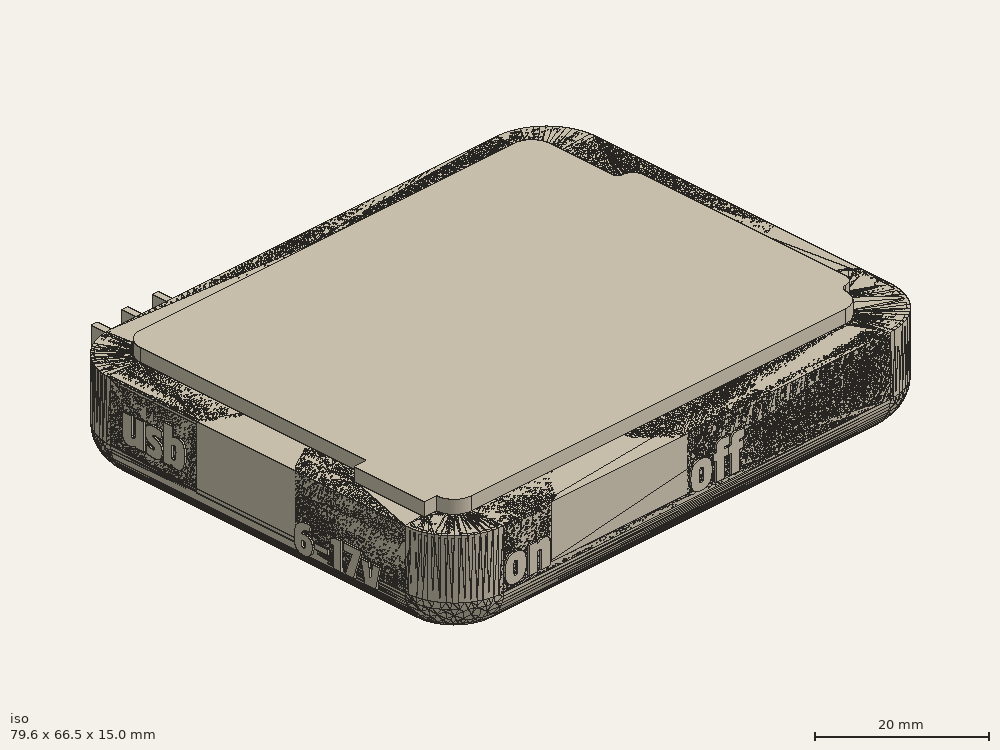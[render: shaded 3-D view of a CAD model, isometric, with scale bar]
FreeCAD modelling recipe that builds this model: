
FCSTD DOCUMENT  (FreeCAD 0.16R6712 (Git))
Label: baseConLetras
License: All rights reserved
LicenseURL: http://en.wikipedia.org/wiki/All_rights_reserved
objects: PartDesign::Fillet×18, Sketcher::SketchObject×15, PartDesign::Pocket×9, Part::Extrusion×7, PartDesign::Pad×6, Part::MultiFuse×6, Part::Cylinder×4, Part::Box×3, PartDesign::Chamfer×2, Part::Cut×1, Mesh::Feature×1, Part::Feature×1, Part::FeaturePython×1, Part::Mirroring×1
note: 89 computed .brp shape members not serialized (recipe doc carries the construction recipe); baked Part::Feature solids carry a one-line shape summary decoded from their .brp

FEATURE [Part::Cylinder] Cylinder  label="Cilindro"
  Angle = 360
  Height = 4.5
  Placement = pos=(-20.32,-24.13,0) rot=(0,0,1;0rad)
  Radius = 1.4
FEATURE [Part::Cylinder] Cylinder001  label="Cilindro001"
  Angle = 360
  Height = 4.5
  Placement = pos=(31.75,-19.05,0) rot=(0,0,1;0rad)
  Radius = 1.4
FEATURE [Part::Cylinder] Cylinder002  label="Cilindro002"
  Angle = 360
  Height = 4.5
  Placement = pos=(31.75,8.9,0) rot=(0,0,1;0rad)
  Radius = 1.4
FEATURE [Part::Cylinder] Cylinder003  label="Cilindro003"
  Angle = 360
  Height = 4.5
  Placement = pos=(-19.05,24.13,0) rot=(0,0,1;0rad)
  Radius = 1.4
FEATURE [Sketcher::SketchObject] Sketch
  Placement = pos=(0,0,3) rot=(0,0,1;0rad)
  sketch-geometry (16):
    g0: LineSegment StartX=-34.59 StartY=-24.13 StartZ=0 EndX=-36.59 EndY=-24.13 EndZ=0
    g1: LineSegment StartX=-36.59 StartY=-24.13 StartZ=0 EndX=-36.59 EndY=-12.63 EndZ=0
    g2: LineSegment StartX=-36.59 StartY=-12.63 StartZ=0 EndX=-34.59 EndY=-12.63 EndZ=0
    g3: LineSegment StartX=-34.59 StartY=-12.63 StartZ=0 EndX=-34.59 EndY=24.13 EndZ=0
    g4: ArcOfCircle CenterX=-31.75 CenterY=24.13 CenterZ=0 NormalX=0 NormalY=0 NormalZ=1 Radius=2.84 StartAngle=1.5708 EndAngle=3.14159
    g5: LineSegment StartX=-31.75 StartY=26.97 StartZ=0 EndX=29.21 EndY=26.97 EndZ=0
    g6: ArcOfCircle CenterX=29.21 CenterY=24.13 CenterZ=0 NormalX=0 NormalY=0 NormalZ=1 Radius=2.84 StartAngle=3.7035e-08 EndAngle=1.5708
    g7: LineSegment StartX=32.05 StartY=24.13 StartZ=0 EndX=32.05 EndY=13.97 EndZ=0
    g8: ArcOfCircle CenterX=33.02 CenterY=13.97 CenterZ=0 NormalX=0 NormalY=0 NormalZ=1 Radius=0.969997 StartAngle=3.14159 EndAngle=4.71239
    g9: ArcOfCircle CenterX=33.02 CenterY=11.43 CenterZ=0 NormalX=0 NormalY=0 NormalZ=1 Radius=1.57 StartAngle=6.28319 EndAngle=7.85398
    g10: LineSegment StartX=34.59 StartY=11.43 StartZ=0 EndX=34.59 EndY=-21.59 EndZ=0
    g11: ArcOfCircle CenterX=33.02 CenterY=-21.59 CenterZ=0 NormalX=0 NormalY=0 NormalZ=1 Radius=1.57 StartAngle=4.71239 EndAngle=6.28319
    g12: ArcOfCircle CenterX=33.02 CenterY=-24.13 CenterZ=0 NormalX=0 NormalY=0 NormalZ=1 Radius=0.97 StartAngle=1.5708 EndAngle=3.1416
    g13: ArcOfCircle CenterX=29.21 CenterY=-24.13 CenterZ=0 NormalX=0 NormalY=0 NormalZ=1 Radius=2.83999 StartAngle=4.71238 EndAngle=6.28319
    g14: LineSegment StartX=29.21 StartY=-26.97 StartZ=0 EndX=-31.75 EndY=-26.97 EndZ=0
    g15: ArcOfCircle CenterX=-31.75 CenterY=-24.13 CenterZ=0 NormalX=0 NormalY=0 NormalZ=1 Radius=2.84 StartAngle=3.14159 EndAngle=4.71239
  constraints (56):
    c: Horizontal(g0)
    c: Coincident(g0,g1)
    c: Vertical(g1)
    c: Coincident(g1,g2)
    c: Horizontal(g2)
    c: Coincident(g2,g3)
    c: Vertical(g3)
    c: Coincident(g4,g3)
    c: DistanceY(g2,g-1) = 12.63
    c: DistanceX(g2,g-1) = 34.59
    c: DistanceY(g-1,g3) = 24.13
    c: Tangent(g3,g4)
    c: DistanceY(g-1,g4) = 26.97
    c: DistanceX(g2,g2) = 2
    c: DistanceY(g1,g1) = 11.5
    c: DistanceX(g0,g0) = 2
    c: Coincident(g5,g4)
    c: Horizontal(g5)
    c: DistanceX(g5,g5) = 60.96
    c: Tangent(g4,g5)
    c: Coincident(g6,g5)
    c: Tangent(g6,g5)
    c: DistanceY(g-1,g6) = 24.13
    c: Coincident(g7,g6)
    c: Vertical(g7)
    c: DistanceY(g7,g7) = 10.16
    c: Tangent(g7,g6)
    c: Coincident(g8,g7)
    c: Coincident(g9,g8)
    c: Tangent(g8,g9)
    c: Tangent(g8,g7)
    c: Coincident(g10,g9)
    c: Vertical(g10)
    c: DistanceX(g-1,g10) = 34.59
    c: DistanceY(g10,g-1) = 21.59
    c: Tangent(g10,g9)
    c: DistanceY(g-1,g9) = 11.43
    c: Coincident(g11,g10)
    c: Coincident(g12,g11)
    c: Coincident(g13,g12)
    c: Tangent(g11,g12)
    c: Tangent(g11,g10)
    c: Tangent(g13,g12)
    c: DistanceX(g7,g8) = 0.97
    c: DistanceX(g11,g10) = 1.57
    c: DistanceX(g12,g11) = 0.97
    c: Radius(g11) = 1.57
    c: DistanceY(g13,g-1) = 26.97
    c: Coincident(g14,g13)
    c: Horizontal(g14)
    c: DistanceX(g14,g-1) = 31.75
    c: Coincident(g15,g14)
    c: Coincident(g15,g0)
    c: Radius(g15) = 2.84
    c: DistanceX(g-1,g13) = 29.21
    c: Tangent(g14,g13)
FEATURE [PartDesign::Pad] Pad  label="placa"
  Length = 10
  Length2 = 100
  Placement = pos=(0,0,3) rot=(0,0,1;0rad)
  Sketch = -> Sketch
  Type = 0
FEATURE [Sketcher::SketchObject] Sketch001
  ExternalGeometry = -> [Pad]
  Placement = pos=(0,0,3) rot=(1,0,0;3.14159rad)
  Support = -> Pad [Face17]
  sketch-geometry (24):
    g0: ArcOfCircle CenterX=29.21 CenterY=24.13 CenterZ=0 NormalX=0 NormalY=0 NormalZ=1 Radius=1.5 StartAngle=6.28318 EndAngle=7.85398
    g1: ArcOfCircle CenterX=31.77 CenterY=19.04 CenterZ=0 NormalX=0 NormalY=0 NormalZ=1 Radius=3 StartAngle=2.27479 EndAngle=4.23644
    g2: ArcOfCircle CenterX=-20.32 CenterY=24.13 CenterZ=0 NormalX=0 NormalY=0 NormalZ=1 Radius=3 StartAngle=3.32443 EndAngle=6.10035
    g3: ArcOfCircle CenterX=-14.9117 CenterY=23.13 CenterZ=0 NormalX=0 NormalY=0 NormalZ=1 Radius=2.5 StartAngle=1.5708 EndAngle=2.95876
    g4: LineSegment StartX=-14.9117 StartY=25.63 StartZ=0 EndX=29.21 EndY=25.63 EndZ=0
    g5: ArcOfCircle CenterX=-31.75 CenterY=24.13 CenterZ=0 NormalX=0 NormalY=0 NormalZ=1 Radius=1.50001 StartAngle=1.5708 EndAngle=3.14159
    g6: LineSegment StartX=-31.75 StartY=25.63 StartZ=0 EndX=-25.7283 EndY=25.63 EndZ=0
    g7: ArcOfCircle CenterX=-25.7283 CenterY=23.13 CenterZ=0 NormalX=0 NormalY=0 NormalZ=1 Radius=2.5 StartAngle=0.182833 EndAngle=1.5708
    g8: LineSegment StartX=-33.25 StartY=24.13 StartZ=0 EndX=-33.25 EndY=-24.13 EndZ=0
    g9: ArcOfCircle CenterX=-31.75 CenterY=-24.13 CenterZ=0 NormalX=0 NormalY=0 NormalZ=1 Radius=1.50001 StartAngle=3.14159 EndAngle=4.71239
    g10: ArcOfCircle CenterX=-19.05 CenterY=-24.13 CenterZ=0 NormalX=0 NormalY=0 NormalZ=1 Radius=3 StartAngle=0.182835 EndAngle=2.95876
    g11: ArcOfCircle CenterX=-24.4583 CenterY=-23.13 CenterZ=0 NormalX=0 NormalY=0 NormalZ=1 Radius=2.5 StartAngle=4.71239 EndAngle=6.10035
    g12: LineSegment StartX=-31.75 StartY=-25.63 StartZ=0 EndX=-24.4583 EndY=-25.63 EndZ=0
    g13: ArcOfCircle CenterX=-13.6417 CenterY=-23.13 CenterZ=0 NormalX=0 NormalY=0 NormalZ=1 Radius=2.5 StartAngle=3.32443 EndAngle=4.71239
    g14: LineSegment StartX=-13.6417 StartY=-25.63 StartZ=0 EndX=29.21 EndY=-25.63 EndZ=0
    g15: ArcOfCircle CenterX=29.21 CenterY=-24.13 CenterZ=0 NormalX=0 NormalY=0 NormalZ=1 Radius=1.5 StartAngle=4.71239 EndAngle=6.28319
    g16: ArcOfCircle CenterX=31.75 CenterY=-8.9 CenterZ=0 NormalX=0 NormalY=0 NormalZ=1 Radius=3 StartAngle=2.04266 EndAngle=4.01315
    g17: ArcOfCircle CenterX=28.21 CenterY=-13.1093 CenterZ=0 NormalX=0 NormalY=0 NormalZ=1 Radius=2.5 StartAngle=6.2812e-08 EndAngle=0.871554
    g18: LineSegment StartX=30.71 StartY=-24.13 StartZ=0 EndX=30.71 EndY=-13.1093 EndZ=0
    g19: ArcOfCircle CenterX=29.25 CenterY=-4.00102 CenterZ=0 NormalX=0 NormalY=0 NormalZ=1 Radius=2.5 StartAngle=5.18425 EndAngle=6.28319
    g20: ArcOfCircle CenterX=29.25 CenterY=14.1513 CenterZ=0 NormalX=0 NormalY=0 NormalZ=1 Radius=2.5 StartAngle=6.28319 EndAngle=7.37804
    g21: LineSegment StartX=31.75 StartY=14.1513 StartZ=0 EndX=31.75 EndY=-4.00102 EndZ=0
    g22: LineSegment StartX=30.71 StartY=24.13 StartZ=0 EndX=30.71 EndY=23.2324 EndZ=0
    g23: ArcOfCircle CenterX=28.21 CenterY=23.2324 CenterZ=0 NormalX=0 NormalY=0 NormalZ=1 Radius=2.5 StartAngle=5.41639 EndAngle=6.28318
  constraints (84):
    c: Coincident(g0,g-3)
    c: Radius(g1) = 3
    c: Radius(g0) = 1.5
    c: DistanceY(g1,g-4) = 2.55
    c: DistanceX(g1,g-4) = 2.82
    c: DistanceY(g-1,g2) = 24.13
    c: DistanceX(g2,g-1) = 20.32
    c: Radius(g2) = 3
    c: Coincident(g3,g2)
    c: Coincident(g4,g3)
    c: Coincident(g4,g0)
    c: Horizontal(g4)
    c: Tangent(g4,g0)
    c: Tangent(g3,g4)
    c: Tangent(g2,g3)
    c: Radius(g3) = 2.5
    c: Coincident(g5,g-6)
    c: PointOnObject(g5,g4)
    c: Tangent(g5,g4) = 1.5708
    c: Coincident(g6,g5)
    c: Horizontal(g6)
    c: Coincident(g7,g2)
    c: Coincident(g7,g6)
    c: Tangent(g7,g2)
    c: Tangent(g6,g7)
    c: Radius(g7) = 2.5
    c: Coincident(g8,g5)
    c: Vertical(g8)
    c: Coincident(g9,g-7)
    c: Coincident(g9,g8)
    c: Tangent(g9,g8)
    c: Tangent(g5,g8)
    c: DistanceY(g10,g-1) = 24.13
    c: DistanceX(g10,g-1) = 19.05
    c: Radius(g10) = 3
    c: Coincident(g11,g10)
    c: Coincident(g12,g9)
    c: Coincident(g12,g11)
    c: Horizontal(g12)
    c: Tangent(g9,g12)
    c: Tangent(g12,g11)
    c: Tangent(g11,g10)
    c: Radius(g11) = 2.5
    c: Coincident(g13,g10)
    c: Tangent(g13,g10)
    c: Coincident(g14,g13)
    c: Horizontal(g14)
    c: Coincident(g15,g-8)
    c: Coincident(g15,g14)
    c: Coincident(g17,g16)
    c: Tangent(g15,g14)
    c: Tangent(g14,g13)
    c: Radius(g15) = 1.5
    c: Radius(g13) = 2.5
    c: Coincident(g18,g15)
    c: Coincident(g18,g17)
    c: Vertical(g18)
    c: Tangent(g15,g18)
    c: DistanceX(g-1,g16) = 31.75
    c: DistanceY(g16,g-1) = 8.9
    c: Tangent(g16,g17)
    c: Tangent(g17,g18)
    c: Radius(g16) = 3
    c: Coincident(g19,g16)
    c: Coincident(g20,g1)
    c: Coincident(g21,g20)
    c: Coincident(g21,g19)
    c: Vertical(g21)
    c: Tangent(g19,g21)
    c: Tangent(g19,g16)
    c: Radius(g19) = 2.5
    c: Radius(g17) = 2.5
    c: Tangent(g20,g21)
    c: Tangent(g20,g1)
    c: Radius(g20) = 2.5
    c: DistanceX(g-1,g20) = 31.75
    c: Coincident(g22,g0)
    c: Vertical(g22)
    c: Tangent(g22,g0)
    c: Coincident(g23,g1)
    c: Coincident(g23,g22)
    c: Tangent(g23,g22)
    c: Tangent(g23,g1)
    c: Radius(g23) = 2.5
FEATURE [PartDesign::Pad] Pad001
  Length = 4
  Length2 = 100
  Placement = pos=(0,0,3) rot=(0,0,1;0rad)
  Sketch = -> Sketch001
  Type = 0
FEATURE [Part::Box] Box  label="Cubo"
  Height = 13
  Length = 79
  Placement = pos=(-39.6,-32,-2) rot=(0,0,1;0rad)
  Width = 64
FEATURE [PartDesign::Fillet] Fillet
  Base = -> Box [Edge7,Edge3,Edge5,Edge1]
  Placement = pos=(-39.6,-32,-2) rot=(0,0,1;0rad)
  Radius = 8
FEATURE [Part::Cut] Cut
  Base = -> Fillet
  Tool = -> Pad001
FEATURE [PartDesign::Chamfer] Chamfer
  Base = -> Cut [Edge4,Edge28,Edge30,Edge32,Edge33,Edge34,Edge35,Edge36]
  Size = 2
FEATURE [PartDesign::Fillet] Fillet001
  Base = -> Chamfer [Edge37,Edge5,Edge2,Edge33,Edge49,Edge51,Edge52,Edge46]
  Radius = 5
FEATURE [PartDesign::Fillet] Fillet002
  Base = -> Fillet001 [Edge155,Edge152,Edge151,Edge148,Edge147,Edge144,Edge143,Edge141,Edge139,Edge137,Edge135,Edge132,Edge130,Edge176,Edge175,Edge173,Edge171,Edge168,Edge167,Edge164,Edge163,Edge160,Edge159,Edge156]
  Radius = 2
FEATURE [PartDesign::Fillet] Fillet003
  Base = -> Fillet002 [Edge83,Edge76,Edge74,Edge79]
  Radius = 0.5
FEATURE [Part::MultiFuse] Fusion
  Shapes = -> [Cylinder003,Cylinder002,Cylinder001,Cylinder]
FEATURE [PartDesign::Fillet] Fillet004  label="tetones"
  Base = -> Fusion [Edge4,Edge10,Edge7,Edge1]
  Radius = 0.5
FEATURE [Mesh::Feature] Icezum_Alhambra_Support_with_text  label="Icezum-Alhambra-Support-with-text"
FEATURE [Part::Feature] Icezum_Alhambra_Support_with_text001
  shape: bbox 75.21 x 82 x 7 mm, 5620 faces, 0 solids (baked)
FEATURE [Sketcher::SketchObject] Sketch002
  Placement = pos=(0,0,11) rot=(0,0,1;0rad)
  Support = -> Fillet003 [Face46]
  sketch-geometry (4):
    g0: LineSegment StartX=-40 StartY=10 StartZ=0 EndX=-33 EndY=6 EndZ=0
    g1: LineSegment StartX=-33 StartY=6 StartZ=0 EndX=-33 EndY=-2 EndZ=0
    g2: LineSegment StartX=-33 StartY=-2 StartZ=0 EndX=-40 EndY=-6 EndZ=0
    g3: LineSegment StartX=-40 StartY=-6 StartZ=0 EndX=-40 EndY=10 EndZ=0
  constraints (12):
    c: Coincident(g0,g1)
    c: Coincident(g1,g2)
    c: Coincident(g2,g3)
    c: Coincident(g3,g0)
    c: Vertical(g1)
    c: Vertical(g3)
    c: DistanceY(g1,g-1) = 2
    c: DistanceY(g-1,g0) = 6
    c: DistanceY(g2,g1) = 4
    c: DistanceY(g0,g0) = 4
    c: DistanceX(g2,g1) = 7
    c: DistanceX(g1,g-1) = 33
FEATURE [PartDesign::Pocket] Pocket  label="usb"
  Length = 9
  Sketch = -> Sketch002
  Type = 0
FEATURE [PartDesign::Fillet] Fillet005
  Base = -> Pocket [Edge120,Edge71,Edge62,Edge68]
  Radius = 0.5
FEATURE [PartDesign::Fillet] Fillet006
  Base = -> Fillet005 [Edge151,Edge178,Edge63]
  Radius = 0.5
FEATURE [Sketcher::SketchObject] Sketch003
  Placement = pos=(0,0,11) rot=(0,0,1;0rad)
  Support = -> Fillet006 [Face2]
  sketch-geometry (4):
    g0: LineSegment StartX=-23 StartY=-32.5 StartZ=0 EndX=-17 EndY=-26 EndZ=0
    g1: LineSegment StartX=-17 StartY=-26 StartZ=0 EndX=-8.5 EndY=-26 EndZ=0
    g2: LineSegment StartX=-8.5 StartY=-26 StartZ=0 EndX=-2.5 EndY=-32.5 EndZ=0
    g3: LineSegment StartX=-2.5 StartY=-32.5 StartZ=0 EndX=-23 EndY=-32.5 EndZ=0
  constraints (12):
    c: Coincident(g0,g1)
    c: Horizontal(g1)
    c: Coincident(g1,g2)
    c: Coincident(g2,g3)
    c: Horizontal(g3)
    c: Coincident(g3,g0)
    c: DistanceX(g0,g-1) = 17
    c: DistanceY(g0,g-1) = 26
    c: DistanceY(g0,g0) = 6.5
    c: DistanceX(g1,g1) = 8.5
    c: DistanceX(g1,g2) = 6
    c: DistanceX(g0,g0) = 6
FEATURE [PartDesign::Pocket] Pocket001
  Length = 8
  Sketch = -> Sketch003
  Type = 0
FEATURE [PartDesign::Fillet] Fillet007
  Base = -> Pocket001 [Edge46,Edge44]
  Radius = 3
FEATURE [PartDesign::Fillet] Fillet008
  Base = -> Fillet007 [Edge32,Edge154]
  Radius = 0.5
FEATURE [Sketcher::SketchObject] Sketch004
  Placement = pos=(0,0,11) rot=(0,0,1;0rad)
  Support = -> Fillet008 [Face22]
  sketch-geometry (4):
    g0: LineSegment StartX=33 StartY=-9 StartZ=0 EndX=40 EndY=-5 EndZ=0
    g1: LineSegment StartX=40 StartY=-5 StartZ=0 EndX=40 EndY=-19 EndZ=0
    g2: LineSegment StartX=40 StartY=-19 StartZ=0 EndX=33 EndY=-15 EndZ=0
    g3: LineSegment StartX=33 StartY=-15 StartZ=0 EndX=33 EndY=-9 EndZ=0
  constraints (12):
    c: Coincident(g0,g1)
    c: Vertical(g1)
    c: Coincident(g1,g2)
    c: Coincident(g2,g3)
    c: Coincident(g3,g0)
    c: Vertical(g3)
    c: DistanceY(g3,g3) = 6
    c: DistanceX(g-1,g2) = 33
    c: DistanceY(g0,g-1) = 9
    c: DistanceY(g0,g0) = 4
    c: DistanceY(g1,g2) = 4
    c: DistanceX(g2,g1) = 7
FEATURE [PartDesign::Pocket] Pocket002
  Length = 5
  Sketch = -> Sketch004
  Type = 0
FEATURE [PartDesign::Fillet] Fillet009
  Base = -> Pocket002 [Edge228,Edge229,Edge227,Edge249,Edge226]
  Radius = 2
FEATURE [PartDesign::Fillet] Fillet010
  Base = -> Fillet009 [Edge20,Edge22,Edge24,Edge15,Edge19]
  Radius = 0.5
FEATURE [Sketcher::SketchObject] Sketch005
  Placement = pos=(0,0,11) rot=(0,0,1;0rad)
  Support = -> Fillet010 [Face23]
  sketch-geometry (12):
    g0: LineSegment StartX=-31.5 StartY=27.3 StartZ=0 EndX=-27.5 EndY=27.3 EndZ=0
    g1: LineSegment StartX=-27.5 StartY=27.3 StartZ=0 EndX=-27.5 EndY=34.3 EndZ=0
    g2: LineSegment StartX=-27.5 StartY=34.3 StartZ=0 EndX=-26.5 EndY=34.3 EndZ=0
    g3: LineSegment StartX=-26.5 StartY=34.3 StartZ=0 EndX=-26.5 EndY=27.3 EndZ=0
    g4: LineSegment StartX=-26.5 StartY=27.3 StartZ=0 EndX=-22.5 EndY=27.3 EndZ=0
    g5: LineSegment StartX=-22.5 StartY=27.3 StartZ=0 EndX=-22.5 EndY=34.3 EndZ=0
    g6: LineSegment StartX=-22.5 StartY=34.3 StartZ=0 EndX=-21.5 EndY=34.3 EndZ=0
    g7: LineSegment StartX=-21.5 StartY=34.3 StartZ=0 EndX=-21.5 EndY=26.8 EndZ=0
    g8: LineSegment StartX=-21.5 StartY=26.8 StartZ=0 EndX=-32.5 EndY=26.8 EndZ=0
    g9: LineSegment StartX=-32.5 StartY=26.8 StartZ=0 EndX=-32.5 EndY=34.3 EndZ=0
    g10: LineSegment StartX=-32.5 StartY=34.3 StartZ=0 EndX=-31.5 EndY=34.3 EndZ=0
    g11: LineSegment StartX=-31.5 StartY=34.3 StartZ=0 EndX=-31.5 EndY=27.3 EndZ=0
  constraints (36):
    c: Horizontal(g0)
    c: Coincident(g0,g1)
    c: Vertical(g1)
    c: Coincident(g1,g2)
    c: Horizontal(g2)
    c: Coincident(g2,g3)
    c: Vertical(g3)
    c: Coincident(g3,g4)
    c: Horizontal(g4)
    c: Coincident(g4,g5)
    c: Vertical(g5)
    c: Coincident(g5,g6)
    c: Horizontal(g6)
    c: Coincident(g6,g7)
    c: Vertical(g7)
    c: Coincident(g7,g8)
    c: Horizontal(g8)
    c: Coincident(g8,g9)
    c: Vertical(g9)
    c: Coincident(g9,g10)
    c: Horizontal(g10)
    c: Coincident(g10,g11)
    c: Coincident(g11,g0)
    c: Vertical(g11)
    c: Equal(g6,g2)
    c: Equal(g2,g10)
    c: Equal(g3,g11)
    c: Equal(g11,g5)
    c: Equal(g9,g7)
    c: DistanceX(g2,g2) = 1
    c: Equal(g4,g0)
    c: DistanceX(g0,g0) = 4
    c: DistanceY(g5,g5) = 7
    c: DistanceY(g7,g7) = 7.5
    c: DistanceX(g7,g-1) = 21.5
    c: DistanceY(g-1,g7) = 26.8
FEATURE [PartDesign::Pocket] Pocket003
  Length = 12.5
  Sketch = -> Sketch005
  Type = 0
FEATURE [Sketcher::SketchObject] Sketch006
  ExternalGeometry = -> [Pocket003]
  Placement = pos=(0,0,11) rot=(0,0,1;0rad)
  Support = -> Pocket003 [Face148]
  sketch-geometry (4):
    g0: LineSegment StartX=-31.5 StartY=32 StartZ=0 EndX=-22.5 EndY=32 EndZ=0
    g1: LineSegment StartX=-22.5 StartY=32 StartZ=0 EndX=-22.5 EndY=27.3 EndZ=0
    g2: LineSegment StartX=-22.5 StartY=27.3 StartZ=0 EndX=-31.5 EndY=27.3 EndZ=0
    g3: LineSegment StartX=-31.5 StartY=27.3 StartZ=0 EndX=-31.5 EndY=32 EndZ=0
  constraints (10):
    c: Coincident(g0,g1)
    c: Coincident(g1,g2)
    c: Coincident(g2,g3)
    c: Coincident(g3,g0)
    c: Horizontal(g0)
    c: Horizontal(g2)
    c: Vertical(g1)
    c: Vertical(g3)
    c: Coincident(g0,g-4)
    c: Coincident(g1,g-3)
FEATURE [PartDesign::Pocket] Pocket004
  Length = 5
  Sketch = -> Sketch006
  Type = 0
FEATURE [Sketcher::SketchObject] Sketch007
  ExternalGeometry = -> [Pocket004]
  Placement = pos=(0,0,-1.5) rot=(0,0,1;0rad)
  Support = -> Pocket004 [Face97]
  sketch-geometry (12):
    g0: LineSegment StartX=-31.5 StartY=32 StartZ=0 EndX=-32.5 EndY=32 EndZ=0
    g1: LineSegment StartX=-32.5 StartY=32 StartZ=0 EndX=-32.5 EndY=26.8 EndZ=0
    g2: LineSegment StartX=-32.5 StartY=26.8 StartZ=0 EndX=-31.5 EndY=26.8 EndZ=0
    g3: LineSegment StartX=-31.5 StartY=26.8 StartZ=0 EndX=-31.5 EndY=32 EndZ=0
    g4: LineSegment StartX=-27.5 StartY=32 StartZ=0 EndX=-26.5 EndY=32 EndZ=0
    g5: LineSegment StartX=-26.5 StartY=32 StartZ=0 EndX=-26.5 EndY=26.8 EndZ=0
    g6: LineSegment StartX=-26.5 StartY=26.8 StartZ=0 EndX=-27.5 EndY=26.8 EndZ=0
    g7: LineSegment StartX=-27.5 StartY=26.8 StartZ=0 EndX=-27.5 EndY=32 EndZ=0
    g8: LineSegment StartX=-21.5 StartY=26.8 StartZ=0 EndX=-22.5 EndY=26.8 EndZ=0
    g9: LineSegment StartX=-22.5 StartY=26.8 StartZ=0 EndX=-22.5 EndY=32 EndZ=0
    g10: LineSegment StartX=-22.5 StartY=32 StartZ=0 EndX=-21.5 EndY=32 EndZ=0
    g11: LineSegment StartX=-21.5 StartY=32 StartZ=0 EndX=-21.5 EndY=26.8 EndZ=0
  constraints (31):
    c: Coincident(g0,g1)
    c: Coincident(g1,g2)
    c: Coincident(g2,g3)
    c: Coincident(g3,g0)
    c: Horizontal(g0)
    c: Horizontal(g2)
    c: Vertical(g1)
    c: Vertical(g3)
    c: Coincident(g0,g-4)
    c: Coincident(g1,g-9)
    c: Coincident(g4,g5)
    c: Coincident(g5,g6)
    c: Coincident(g6,g7)
    c: Coincident(g7,g4)
    c: Horizontal(g4)
    c: Horizontal(g6)
    c: Vertical(g5)
    c: Vertical(g7)
    c: Coincident(g4,g-5)
    c: PointOnObject(g5,g-9)
    c: Coincident(g8,g9)
    c: Coincident(g9,g10)
    c: Coincident(g10,g11)
    c: Coincident(g11,g8)
    c: Horizontal(g8)
    c: Horizontal(g10)
    c: Vertical(g9)
    c: Vertical(g11)
    c: Coincident(g8,g-9)
    c: Coincident(g9,g-7)
    c: Coincident(g4,g-6)
FEATURE [PartDesign::Pocket] Pocket005
  Length = 5
  Sketch = -> Sketch007
  Type = 1
FEATURE [PartDesign::Fillet] Fillet011
  Base = -> Pocket005 [Edge382,Edge394,Edge380,Edge392,Edge261,Edge277,Edge378,Edge379,Edge375,Edge376,Edge288,Edge286]
  Radius = 1
FEATURE [PartDesign::Fillet] Fillet012
  Base = -> Fillet011 [Edge430,Edge431,Edge427,Edge309,Edge306,Edge429,Edge440,Edge441,Edge437,Edge322,Edge319,Edge439]
  Radius = 1
FEATURE [Sketcher::SketchObject] Sketch008
  ExternalGeometry = -> [Fillet012]
  Placement = pos=(0,0,11) rot=(0,0,1;0rad)
  Support = -> Fillet012 [Face145]
  sketch-geometry (12):
    g0: LineSegment StartX=-10 StartY=26.97 StartZ=0 EndX=-3 EndY=26.97 EndZ=0
    g1: LineSegment StartX=-3 StartY=26.97 StartZ=0 EndX=-3 EndY=29.97 EndZ=0
    g2: LineSegment StartX=-3 StartY=29.97 StartZ=0 EndX=-10 EndY=29.97 EndZ=0
    g3: LineSegment StartX=-10 StartY=29.97 StartZ=0 EndX=-10 EndY=26.97 EndZ=0
    g4: LineSegment StartX=13 StartY=26.97 StartZ=0 EndX=20 EndY=26.97 EndZ=0
    g5: LineSegment StartX=20 StartY=26.97 StartZ=0 EndX=20 EndY=29.97 EndZ=0
    g6: LineSegment StartX=20 StartY=29.97 StartZ=0 EndX=13 EndY=29.97 EndZ=0
    g7: LineSegment StartX=13 StartY=29.97 StartZ=0 EndX=13 EndY=26.97 EndZ=0
    g8: LineSegment StartX=0 StartY=-26.97 StartZ=0 EndX=7 EndY=-26.97 EndZ=0
    g9: LineSegment StartX=7 StartY=-26.97 StartZ=0 EndX=7 EndY=-29.97 EndZ=0
    g10: LineSegment StartX=7 StartY=-29.97 StartZ=0 EndX=0 EndY=-29.97 EndZ=0
    g11: LineSegment StartX=0 StartY=-29.97 StartZ=0 EndX=0 EndY=-26.97 EndZ=0
  constraints (36):
    c: Coincident(g0,g1)
    c: Coincident(g1,g2)
    c: Coincident(g2,g3)
    c: Coincident(g3,g0)
    c: Horizontal(g0)
    c: Horizontal(g2)
    c: Vertical(g1)
    c: Vertical(g3)
    c: PointOnObject(g0,g-3)
    c: Coincident(g4,g5)
    c: Coincident(g5,g6)
    c: Coincident(g6,g7)
    c: Coincident(g7,g4)
    c: Horizontal(g4)
    c: Horizontal(g6)
    c: Vertical(g5)
    c: Vertical(g7)
    c: PointOnObject(g4,g-3)
    c: Coincident(g8,g9)
    c: Coincident(g9,g10)
    c: Coincident(g10,g11)
    c: Coincident(g11,g8)
    c: Horizontal(g8)
    c: Horizontal(g10)
    c: Vertical(g9)
    c: Vertical(g11)
    c: PointOnObject(g8,g-4)
    c: Equal(g2,g6)
    c: Equal(g6,g10)
    c: DistanceX(g10,g10) = 7
    c: Equal(g1,g7)
    c: Equal(g7,g11)
    c: DistanceY(g9,g9) = 3
    c: DistanceX(g0,g-1) = 3
    c: DistanceX(g0,g4) = 23
    c: PointOnObject(g8,g-2)
FEATURE [PartDesign::Pocket] Pocket006
  Length = 10
  Sketch = -> Sketch008
  Type = 0
FEATURE [Sketcher::SketchObject] Sketch009
  Placement = pos=(-9,0,0) rot=(0.57735,0.57735,0.57735;2.0944rad)
  sketch-geometry (7):
    g0: LineSegment StartX=27.5 StartY=-1 StartZ=0 EndX=27.5 EndY=4 EndZ=0
    g1: LineSegment StartX=27.5 StartY=4 StartZ=0 EndX=26.5 EndY=5 EndZ=0
    g2: LineSegment StartX=26.5 StartY=5 StartZ=0 EndX=26.5 EndY=6 EndZ=0
    g3: LineSegment StartX=26.5 StartY=6 StartZ=0 EndX=27.5 EndY=7 EndZ=0
    g4: LineSegment StartX=27.5 StartY=7 StartZ=0 EndX=28.5 EndY=7 EndZ=0
    g5: LineSegment StartX=28.5 StartY=7 StartZ=0 EndX=28.5 EndY=-1 EndZ=0
    g6: LineSegment StartX=28.5 StartY=-1 StartZ=0 EndX=27.5 EndY=-1 EndZ=0
  constraints (21):
    c: Vertical(g0)
    c: Coincident(g0,g1)
    c: Coincident(g1,g2)
    c: Vertical(g2)
    c: Coincident(g2,g3)
    c: Coincident(g3,g4)
    c: Coincident(g4,g5)
    c: Vertical(g5)
    c: Coincident(g5,g6)
    c: Coincident(g6,g0)
    c: Horizontal(g6)
    c: DistanceX(g1,g0) = 1
    c: DistanceY(g0,g0) = 5
    c: Angle(g1,g2) = 2.35619
    c: Perpendicular(g1,g3)
    c: DistanceY(g2,g2) = 1
    c: Horizontal(g4)
    c: DistanceX(g6,g6) = 1
    c: Equal(g3,g1)
    c: DistanceX(g-1,g0) = 27.5
    c: DistanceY(g0,g-1) = 1
FEATURE [PartDesign::Pad] Pad002
  Length = 5
  Length2 = 100
  Placement = pos=(-9,0,0) rot=(0.57735,0.57735,0.57735;2.0944rad)
  Sketch = -> Sketch009
  Type = 0
FEATURE [Part::FeaturePython] Clone  label="Clone of Pad002"  # Draft clone (typed FeaturePython)
  Objects = -> [Pad002]
  Placement = pos=(14,0,0) rot=(0.57735,0.57735,0.57735;2.0944rad)
  Scale = (1,1,1)
FEATURE [Part::Mirroring] Part__Mirroring  label="Clone of Pad002 (Mirror #1)"
  Base = (0,0,0)
  Normal = (0,1,0)
  Placement = pos=(-13,0,0) rot=(0,0,1;0rad)
  Source = -> Clone
FEATURE [Part::MultiFuse] Fusion001  label="lenguetas"
  Shapes = -> [Part__Mirroring,Pad002,Clone]
FEATURE [Part::MultiFuse] Fusion002
  Shapes = -> [Fusion001,Pocket006]
FEATURE [Sketcher::SketchObject] Sketch010
  ExternalGeometry = -> [Fusion002]
  Placement = pos=(0,0,11) rot=(0,0,1;0rad)
  Support = -> Fusion002 [Face156]
  sketch-geometry (4):
    g0: LineSegment StartX=-41.09 StartY=-13.13 StartZ=0 EndX=-35.09 EndY=-13.13 EndZ=0
    g1: LineSegment StartX=-35.09 StartY=-13.13 StartZ=0 EndX=-35.09 EndY=-23.63 EndZ=0
    g2: LineSegment StartX=-35.09 StartY=-23.63 StartZ=0 EndX=-41.09 EndY=-23.63 EndZ=0
    g3: LineSegment StartX=-41.09 StartY=-23.63 StartZ=0 EndX=-41.09 EndY=-13.13 EndZ=0
  constraints (12):
    c: Coincident(g0,g1)
    c: Coincident(g1,g2)
    c: Coincident(g2,g3)
    c: Coincident(g3,g0)
    c: Horizontal(g0)
    c: Horizontal(g2)
    c: Vertical(g1)
    c: Vertical(g3)
    c: DistanceY(g-4,g1) = 0.5
    c: DistanceY(g0,g-3) = 0.5
    c: PointOnObject(g-3,g1)
    c: DistanceX(g0,g0) = 6
FEATURE [PartDesign::Pocket] Pocket007
  Length = 6
  Sketch = -> Sketch010
  Type = 0
FEATURE [PartDesign::Fillet] Fillet013
  Base = -> Pocket007 [Edge464,Edge461]
  Radius = 4
FEATURE [PartDesign::Fillet] Fillet014
  Base = -> Fillet013 [Edge99,Edge97,Edge95,Edge94,Edge7]
  Radius = 1
FEATURE [PartDesign::Fillet] Fillet015
  Base = -> Fillet014 [Edge214,Edge248,Edge252,Edge204,Edge194,Edge191,Edge186,Edge167,Edge179,Edge176,Edge161,Edge158,Edge153,Edge150,Edge145,Edge139,Edge24,Edge156,Edge17,Edge11,Edge18,Edge4,Edge19,Edge13,Edge20,Edge21,Edge22,Edge23,Edge25]
  Radius = 0.4
FEATURE [Part::MultiFuse] Fusion003
  Shapes = -> [Fillet004,Fillet015]
FEATURE [Sketcher::SketchObject] Sketch011
  ExternalGeometry = -> [Fusion003]
  Placement = pos=(-10,0,0) rot=(0.57735,0.57735,0.57735;2.0944rad)
  Support = -> Fusion003 [Face139]
  sketch-geometry (4):
    g0: ArcOfCircle CenterX=27.37 CenterY=10.6 CenterZ=0 NormalX=0 NormalY=0 NormalZ=1 Radius=0.4 StartAngle=1.5708 EndAngle=3.92701
    g1: LineSegment StartX=27.0872 StartY=10.3172 StartZ=0 EndX=30.97 EndY=6.43431 EndZ=0
    g2: LineSegment StartX=30.97 StartY=6.43431 StartZ=0 EndX=30.97 EndY=11 EndZ=0
    g3: LineSegment StartX=27.37 StartY=11 StartZ=0 EndX=30.97 EndY=11 EndZ=0
  constraints (11):
    c: Coincident(g0,g-4)
    c: Coincident(g0,g-4)
    c: Coincident(g1,g0)
    c: Coincident(g2,g1)
    c: Vertical(g2)
    c: Coincident(g3,g0)
    c: Coincident(g3,g2)
    c: Horizontal(g3)
    c: DistanceX(g-3,g2) = 1
    c: Angle(g2,g1) = 0.785398
    c: Tangent(g1,g0)
FEATURE [PartDesign::Pad] Pad003
  Length = 31
  Length2 = 100
  Sketch = -> Sketch011
  Type = 0
FEATURE [Sketcher::SketchObject] Sketch012
  ExternalGeometry = -> [Pad003]
  Placement = pos=(0,0,0) rot=(0.57735,0.57735,0.57735;2.0944rad)
  Support = -> Pad003 [Face94]
  sketch-geometry (4):
    g0: ArcOfCircle CenterX=-27.37 CenterY=10.6 CenterZ=0 NormalX=0 NormalY=0 NormalZ=1 Radius=0.4 StartAngle=5.49781 EndAngle=7.85398
    g1: LineSegment StartX=-27.0872 StartY=10.3172 StartZ=0 EndX=-29.97 EndY=7.43431 EndZ=0
    g2: LineSegment StartX=-27.37 StartY=11 StartZ=0 EndX=-29.97 EndY=11 EndZ=0
    g3: LineSegment StartX=-29.97 StartY=11 StartZ=0 EndX=-29.97 EndY=7.43431 EndZ=0
  constraints (10):
    c: Coincident(g0,g-4)
    c: Coincident(g0,g-4)
    c: Coincident(g1,g0)
    c: Coincident(g2,g0)
    c: Coincident(g2,g-3)
    c: Coincident(g3,g2)
    c: Coincident(g3,g1)
    c: Tangent(g1,g0)
    c: Angle(g1,g3) = 0.785398
    c: Vertical(g3)
FEATURE [PartDesign::Pad] Pad004
  Length = 10
  Length2 = 100
  Sketch = -> Sketch012
  Type = 0
FEATURE [Sketcher::SketchObject] Sketch013
  ExternalGeometry = -> [Pad004]
  Placement = pos=(0,0,3) rot=(0,0,1;0rad)
  Support = -> Pad004 [Face4]
  sketch-geometry (6):
    g0: ArcOfCircle CenterX=31.77 CenterY=-19.04 CenterZ=0 NormalX=0 NormalY=0 NormalZ=1 Radius=3 StartAngle=1.44865 EndAngle=2.04675
    g1: ArcOfCircle CenterX=32.4021 CenterY=-13.8908 CenterZ=0 NormalX=0 NormalY=0 NormalZ=1 Radius=2.18787 StartAngle=4.59024 EndAngle=6.28319
    g2: LineSegment StartX=34.59 StartY=-13.8908 StartZ=0 EndX=34.59 EndY=3.75328 EndZ=0
    g3: ArcOfCircle CenterX=31.75 CenterY=8.9 CenterZ=0 NormalX=0 NormalY=0 NormalZ=1 Radius=3 StartAngle=4.24053 EndAngle=4.83843
    g4: ArcOfCircle CenterX=32.4021 CenterY=3.75328 CenterZ=0 NormalX=0 NormalY=0 NormalZ=1 Radius=2.18787 StartAngle=7.32987e-07 EndAngle=1.69683
    g5: LineSegment StartX=30.3864 StartY=6.22783 StartZ=0 EndX=30.3955 EndY=-16.3734 EndZ=0
  constraints (17):
    c: Coincident(g0,g-4)
    c: Coincident(g0,g-4)
    c: Coincident(g1,g0)
    c: Coincident(g1,g-5)
    c: Tangent(g0,g1)
    c: Tangent(g1,g-5) = 1.5708
    c: Coincident(g2,g1)
    c: Vertical(g2)
    c: Coincident(g3,g-3)
    c: Coincident(g3,g-3)
    c: Coincident(g4,g3)
    c: Coincident(g4,g2)
    c: Tangent(g4,g3)
    c: Tangent(g4,g2)
    c: Equal(g4,g1)
    c: Coincident(g5,g3)
    c: Coincident(g5,g0)
FEATURE [PartDesign::Pocket] Pocket008
  Length = 2.25
  Sketch = -> Sketch013
  Type = 0
FEATURE [Part::Box] Box001  label="Cubo001"
  Height = 2
  Length = 4
  Placement = pos=(-31.5,27.3,5) rot=(0,0,1;0rad)
  Width = 4.7
FEATURE [Part::Box] Box002  label="Cubo002"
  Height = 2
  Length = 4
  Placement = pos=(-26.5,27.3,5) rot=(0,0,1;0rad)
  Width = 4.7
FEATURE [PartDesign::Fillet] Fillet016
  Base = -> Box001 [Edge7,Edge3,Edge12,Edge2,Edge6]
  Placement = pos=(-31.5,27.3,5) rot=(0,0,1;0rad)
  Radius = 1
FEATURE [PartDesign::Fillet] Fillet017
  Base = -> Box002 [Edge3,Edge7,Edge12,Edge2,Edge6]
  Placement = pos=(-26.5,27.3,5) rot=(0,0,1;0rad)
  Radius = 1
FEATURE [Part::MultiFuse] Fusion004
  Shapes = -> [Pocket008,Fillet016,Fillet017]
FEATURE [Sketcher::SketchObject] Sketch014
  ExternalGeometry = -> [Fusion004]
  Placement = pos=(0,0,-1.5) rot=(0,0,1;0rad)
  Support = -> Fusion004 [Face229]
  sketch-geometry (8):
    g0: LineSegment StartX=-31.5 StartY=26.8 StartZ=0 EndX=-27.5 EndY=26.8 EndZ=0
    g1: LineSegment StartX=-27.5 StartY=26.8 StartZ=0 EndX=-27.5 EndY=27.3 EndZ=0
    g2: LineSegment StartX=-27.5 StartY=27.3 StartZ=0 EndX=-31.5 EndY=27.3 EndZ=0
    g3: LineSegment StartX=-31.5 StartY=27.3 StartZ=0 EndX=-31.5 EndY=26.8 EndZ=0
    g4: LineSegment StartX=-26.5 StartY=27.3 StartZ=0 EndX=-22.5 EndY=27.3 EndZ=0
    g5: LineSegment StartX=-22.5 StartY=27.3 StartZ=0 EndX=-22.5 EndY=26.8 EndZ=0
    g6: LineSegment StartX=-22.5 StartY=26.8 StartZ=0 EndX=-26.5 EndY=26.8 EndZ=0
    g7: LineSegment StartX=-26.5 StartY=26.8 StartZ=0 EndX=-26.5 EndY=27.3 EndZ=0
  constraints (20):
    c: Coincident(g0,g1)
    c: Coincident(g1,g2)
    c: Coincident(g2,g3)
    c: Coincident(g3,g0)
    c: Horizontal(g0)
    c: Horizontal(g2)
    c: Vertical(g1)
    c: Vertical(g3)
    c: Coincident(g0,g-3)
    c: Coincident(g1,g-4)
    c: Coincident(g4,g5)
    c: Coincident(g5,g6)
    c: Coincident(g6,g7)
    c: Coincident(g7,g4)
    c: Horizontal(g4)
    c: Horizontal(g6)
    c: Vertical(g5)
    c: Vertical(g7)
    c: Coincident(g4,g-5)
    c: Coincident(g5,g-6)
FEATURE [PartDesign::Pad] Pad005
  Length = 0.5
  Length2 = 100
  Sketch = -> Sketch014
  Type = 0
FEATURE [Part::Extrusion] Extrude008
  Dir = (0,1,0)
  Solid = false
FEATURE [Part::Extrusion] Extrude006
  Dir = (0,1,0)
  Placement = pos=(0,0,1) rot=(0,0,1;0rad)
  Solid = true
FEATURE [Part::Extrusion] Extrude005
  Dir = (0,1,0)
  Placement = pos=(0,0,1) rot=(0,0,1;0rad)
  Solid = true
FEATURE [Part::Extrusion] Extrude004  label="reset"
  Dir = (0.75,0,0)
  Solid = true
FEATURE [Part::Extrusion] Extrude003  label="off"
  Dir = (0,-1,0)
  Solid = true
FEATURE [Part::Extrusion] Extrude002  label="on"
  Dir = (0,-1,0)
  Solid = false
FEATURE [Part::Extrusion] Extrude001  label="usb001"
  Dir = (-1,0,0)
  Solid = true
FEATURE [PartDesign::Chamfer] Chamfer001  label="6-17v"
  Base = -> Fillet016 [Edge20,Edge82,Edge106,Edge127]
  Size = 0.2
FEATURE [Part::MultiFuse] Fusion005
  Shapes = -> [Chamfer001,Extrude001,Extrude002,Extrude003,Extrude004,Extrude008,Extrude006,Extrude005,Pad005]
